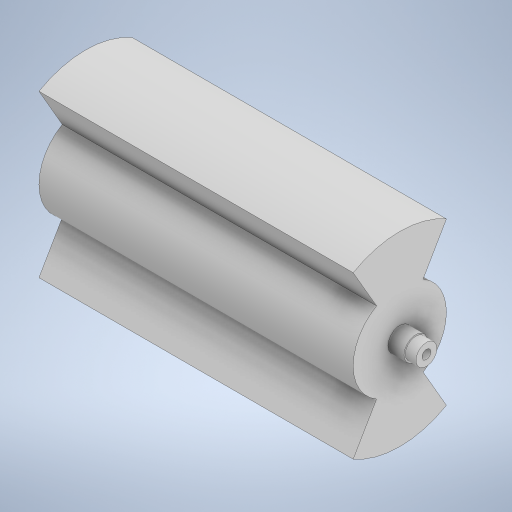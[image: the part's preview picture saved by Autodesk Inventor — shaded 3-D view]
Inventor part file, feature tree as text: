
AUTODESK INVENTOR PART (.ipt)
format: ipt  version: 2024.2 (Build 282272000, 272)  size: 448,512 bytes
history: native  units: in
note: dims shown in document units (in); Inventor stores cm internally (conversion verified against a paired STEP export)
features: extrude x8, sketch x8, mirror x2
ambient origin geometry x8: Origin, YZ Plane, XZ Plane, XY Plane, X Axis, Y Axis, Z Axis, Center Point
bodies: Solid1 (feature_tree)
feature tree (18):
  extrude  "Extrusion1"  Depth=4.6457in TaperAngle=0.0deg
  extrude  "Extrusion2"  Depth=0.6299in TaperAngle=0.0deg
  extrude  "Extrusion3"  Depth=0.1654in TaperAngle=0.0deg
  extrude  "Extrusion4"  Depth=0.3937in TaperAngle=0.0deg
  extrude  "Extrusion8"  TaperAngle=30.0deg  [1 undecoded]
  extrude  "Extrusion9"  Depth=0.3091in
  extrude  "Extrusion11"  Depth=0.7874in TaperAngle=0.0deg
  extrude  "Extrusion10"  Depth=0.2362in TaperAngle=0.0deg
  mirror  "Mirror1"
  mirror  "Mirror2"
  sketch  "Sketch1"  dims[d1=1.378in d2=4.6457in d3=0.0in]
  sketch  "Sketch2"  dims[d4=1.0945in d5=0.6299in d6=0.0in]
  sketch  "Sketch3"  dims[d7=0.3819in d8=0.1654in d9=0.0in]
  sketch  "Sketch4"  dims[d10=0.1339in d11=0.3937in d12=0.0in]
  sketch  "Sketch9"  dims[d32=2.7559in d33=30.0deg]
  sketch  "Sketch10"  dims[d34=5.2756in d35=0.0in d36=0.3091in]
  sketch  "Sketch11"  dims[d37=0.3937in d38=0.0in d39=0.7874in d40=0.0in]
  sketch  "Sketch12"  dims[d42=0.35in d43=0.2362in d44=0.0in]
note: 1 required parameter value undecoded (feature->parameter linkage not recoverable at this tier; creation-order binding heuristic only, values carry confidence <= 0.55)
